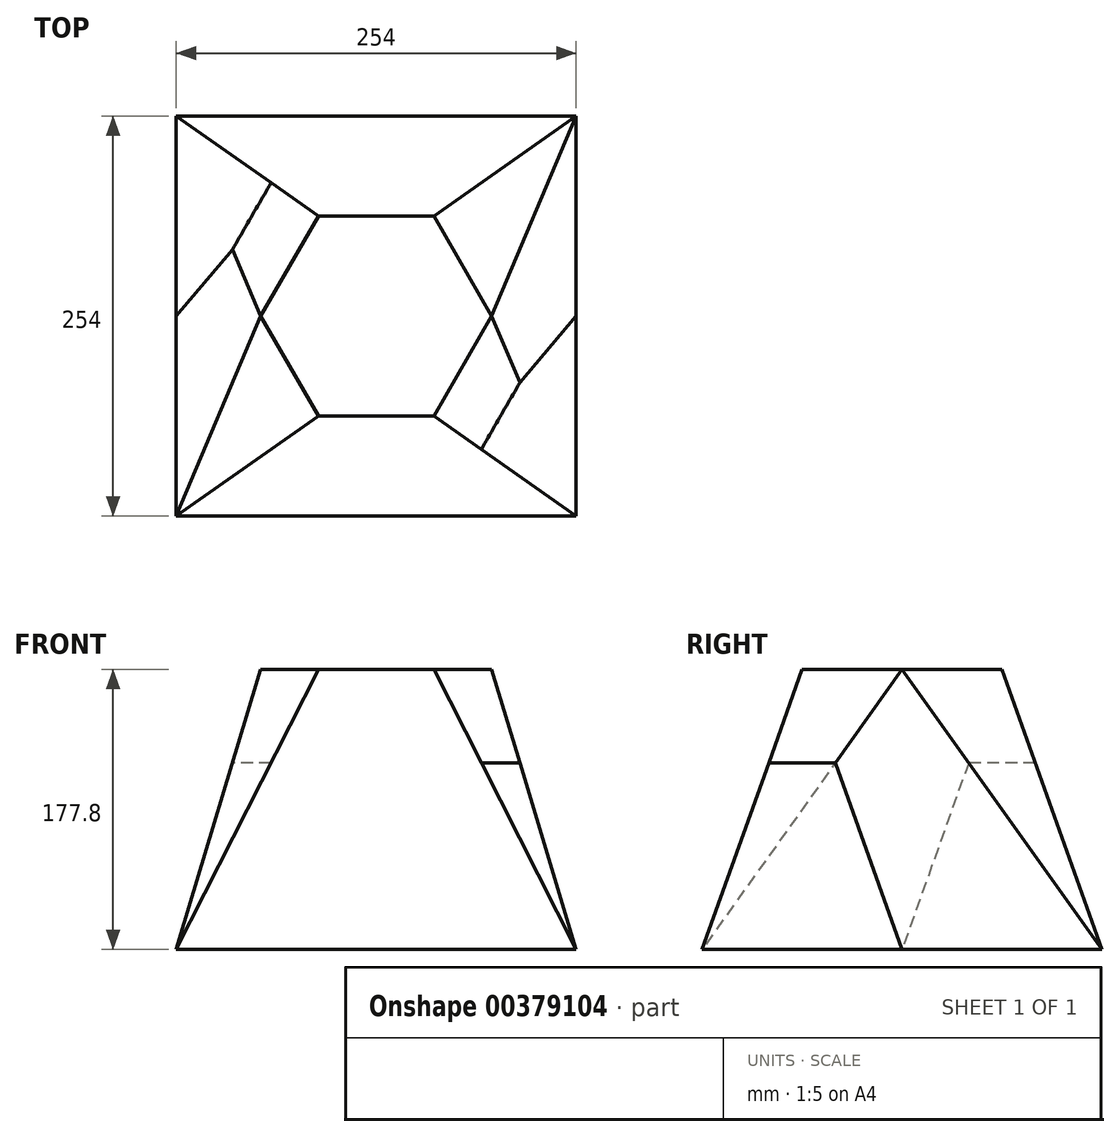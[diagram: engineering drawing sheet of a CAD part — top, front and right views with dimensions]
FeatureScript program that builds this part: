
annotation { "Feature Type Name" : "Feature", "Feature Type Description" : "" }
export const myFeature = defineFeature(function(context is Context, id is Id, definition is map)
    precondition{}
    {
        {
            var Q0;
            Q0=qCreatedBy(makeId("Top.planeOp"),FACE);
            var sketch = newSketch(context, id + "F0", { "sketchPlane" : qUnion([Q0])});
            skLineSegment(sketch, "E0.bottom", {"start": v(-127, 127) * mm, "end": v(127, 127) * mm});
            skLineSegment(sketch, "E0.top", {"start": v(-127, -127) * mm, "end": v(127, -127) * mm});
            skLineSegment(sketch, "E0.left", {"start": v(-127, 127) * mm, "end": v(-127, -127) * mm});
            skLineSegment(sketch, "E0.right", {"start": v(127, 127) * mm, "end": v(127, -127) * mm});
            skSolve(sketch);
        }
        {
            var Q0;
            Q0=makeQuery(id+"F0.imprint","IMPRINT",FACE,{"disambiguationData":[TD([[makeQuery(id+"F0.imprint","IMPRINT",EDGE,{"derivedFrom":sQuery(id+"F0.wireOp",EDGE,"E0.bottom")}),-1.0]])]});
            cPlane(context, id + "F1", {"entities" : qUnion([Q0]), "cplaneType" : CPlaneType.OFFSET, "offset" : 177.8 * mm, "width" : 152.4 * mm, "height" : 152.4 * mm});
        }
        {
            var Q0;
            Q0=qCreatedBy(id+"F1.planeOp",FACE);
            var sketch = newSketch(context, id + "F2", { "sketchPlane" : qUnion([Q0])});
            skCircle(sketch, "E1.cCircle", {"center": v(0, 0) * mm, "radius": 63.5 * mm, "construction": true});
            skLineSegment(sketch, "E1.0", {"start": v(36.66, -63.5) * mm, "end": v(-36.66, -63.5) * mm});
            skLineSegment(sketch, "E1.1", {"start": v(-36.66, -63.5) * mm, "end": v(-73.32, 0) * mm, "construction": true});
            skLineSegment(sketch, "E1.2", {"start": v(-73.32, 0) * mm, "end": v(-36.66, 63.5) * mm, "construction": true});
            skLineSegment(sketch, "E1.3", {"start": v(-36.66, 63.5) * mm, "end": v(36.66, 63.5) * mm});
            skLineSegment(sketch, "E1.4", {"start": v(36.66, 63.5) * mm, "end": v(73.32, 0) * mm, "construction": true});
            skLineSegment(sketch, "E1.5", {"start": v(73.32, 0) * mm, "end": v(36.66, -63.5) * mm, "construction": true});
            skPoint(sketch, "E1.0.midPoint", {"position": v(0, -63.5) * mm});
            skLineSegment(sketch, "E2.bottom", {"start": v(73.32, -63.5) * mm, "end": v(-73.32, -63.5) * mm});
            skLineSegment(sketch, "E2.top", {"start": v(73.32, 63.5) * mm, "end": v(-73.32, 63.5) * mm});
            skLineSegment(sketch, "E2.left", {"start": v(73.32, -63.5) * mm, "end": v(73.32, 63.5) * mm});
            skLineSegment(sketch, "E2.right", {"start": v(-73.32, -63.5) * mm, "end": v(-73.32, 63.5) * mm});
            skSolve(sketch);
        }
        {
            var Q0;
            {var subQ0=sQuery(id+"F2.wireOp",EDGE,"E2.left");Q0=makeQuery(id+"F2.imprint","IMPRINT",FACE,{"disambiguationData":[TD([[makeQuery(id+"F2.imprint","IMPRINT",EDGE,{"derivedFrom":subQ0}),1.0]])]});}
            var Q1;
            Q1=makeQuery(id+"F0.imprint","IMPRINT",FACE,{"disambiguationData":[TD([[makeQuery(id+"F0.imprint","IMPRINT",EDGE,{"derivedFrom":sQuery(id+"F0.wireOp",EDGE,"E0.bottom")}),-1.0]])]});
            loft(context, id + "F3", {"sheetProfilesArray" : [{ "sheetProfileEntities" : qUnion([Q0]) }, { "sheetProfileEntities" : qUnion([Q1]) }]});
        }
        {
            var Q0;
            Q0=qCreatedBy(id+"F1.planeOp",FACE);
            var sketch = newSketch(context, id + "F4", { "sketchPlane" : qUnion([Q0])});
            skCircle(sketch, "E3.cCircle", {"center": v(0, 0) * mm, "radius": 63.5 * mm, "construction": true});
            skLineSegment(sketch, "E3.0", {"start": v(36.66, -63.5) * mm, "end": v(-36.66, -63.5) * mm});
            skLineSegment(sketch, "E3.1", {"start": v(-36.66, -63.5) * mm, "end": v(-73.32, 0) * mm});
            skLineSegment(sketch, "E3.2", {"start": v(-73.32, 0) * mm, "end": v(-36.66, 63.5) * mm});
            skLineSegment(sketch, "E3.3", {"start": v(-36.66, 63.5) * mm, "end": v(36.66, 63.5) * mm});
            skLineSegment(sketch, "E3.4", {"start": v(36.66, 63.5) * mm, "end": v(73.32, 0) * mm});
            skLineSegment(sketch, "E3.5", {"start": v(73.32, 0) * mm, "end": v(36.66, -63.5) * mm});
            skPoint(sketch, "E3.0.midPoint", {"position": v(0, -63.5) * mm});
            skLineSegment(sketch, "E4.bottom", {"start": v(73.32, -63.5) * mm, "end": v(-73.32, -63.5) * mm});
            skLineSegment(sketch, "E4.top", {"start": v(73.32, 63.5) * mm, "end": v(-73.32, 63.5) * mm});
            skLineSegment(sketch, "E4.left", {"start": v(73.32, -63.5) * mm, "end": v(73.32, 63.5) * mm});
            skLineSegment(sketch, "E4.right", {"start": v(-73.32, -63.5) * mm, "end": v(-73.32, 63.5) * mm});
            skSolve(sketch);
        }
        {
            var Q1;
            {var subQ0=sQuery(id+"F4.wireOp",EDGE,"E3.4");Q1=makeQuery(id+"F4.imprint","IMPRINT",FACE,{"disambiguationData":[TD([[makeQuery(id+"F4.imprint","IMPRINT",EDGE,{"derivedFrom":subQ0}),1.0]])]});}
            var Q2;
            Q2=sQuery(id+"F0.wireOp",VERTEX,"E0.right.start");
            loft(context, id + "F5", {"sheetProfilesArray" : [{ "sheetProfileEntities" : qUnion([Q1]) }, { "sheetProfileEntities" : qUnion([Q2]) }]});
        }
        {
            var Q1;
            {var subQ0=sQuery(id+"F4.wireOp",EDGE,"E3.2");Q1=makeQuery(id+"F4.imprint","IMPRINT",FACE,{"disambiguationData":[TD([[makeQuery(id+"F4.imprint","IMPRINT",EDGE,{"derivedFrom":subQ0}),1.0]])]});}
            var Q2;
            Q2=sQuery(id+"F0.wireOp",VERTEX,"E0.left.start");
            loft(context, id + "F6", {"sheetProfilesArray" : [{ "sheetProfileEntities" : qUnion([Q1]) }, { "sheetProfileEntities" : qUnion([Q2]) }]});
        }
        {
            var Q1;
            {var subQ0=sQuery(id+"F4.wireOp",EDGE,"E3.1");Q1=makeQuery(id+"F4.imprint","IMPRINT",FACE,{"disambiguationData":[TD([[makeQuery(id+"F4.imprint","IMPRINT",EDGE,{"derivedFrom":subQ0}),1.0]])]});}
            var Q2;
            Q2=sQuery(id+"F0.wireOp",VERTEX,"E0.left.end");
            loft(context, id + "F7", {"sheetProfilesArray" : [{ "sheetProfileEntities" : qUnion([Q1]) }, { "sheetProfileEntities" : qUnion([Q2]) }]});
        }
        {
            var Q1;
            {var subQ0=sQuery(id+"F4.wireOp",EDGE,"E3.5");Q1=makeQuery(id+"F4.imprint","IMPRINT",FACE,{"disambiguationData":[TD([[makeQuery(id+"F4.imprint","IMPRINT",EDGE,{"derivedFrom":subQ0}),1.0]])]});}
            var Q2;
            Q2=sQuery(id+"F0.wireOp",VERTEX,"E0.right.end");
            loft(context, id + "F8", {"sheetProfilesArray" : [{ "sheetProfileEntities" : qUnion([Q1]) }, { "sheetProfileEntities" : qUnion([Q2]) }]});
        }
        {
            var Q0;
            {var subQ0=sQuery(id+"F4.wireOp",EDGE,"E3.4");Q0=makeQuery(id+"F5.opLoft","SWEPT_BODY",BODY,{"disambiguationData":[OSD([sQuery(id+"F0.wireOp",VERTEX,"E0.right.start"),makeQuery(id+"F4.imprint","IMPRINT",FACE,{"disambiguationData":[TD([[makeQuery(id+"F4.imprint","IMPRINT",EDGE,{"derivedFrom":subQ0}),1.0]])]})])]});}
            var Q1;
            {var subQ0=sQuery(id+"F4.wireOp",EDGE,"E3.2");Q1=makeQuery(id+"F6.opLoft","SWEPT_BODY",BODY,{"disambiguationData":[OSD([sQuery(id+"F0.wireOp",VERTEX,"E0.left.start"),makeQuery(id+"F4.imprint","IMPRINT",FACE,{"disambiguationData":[TD([[makeQuery(id+"F4.imprint","IMPRINT",EDGE,{"derivedFrom":subQ0}),1.0]])]})])]});}
            var Q2;
            {var subQ0=sQuery(id+"F4.wireOp",EDGE,"E3.1");Q2=makeQuery(id+"F7.opLoft","SWEPT_BODY",BODY,{"disambiguationData":[OSD([sQuery(id+"F0.wireOp",VERTEX,"E0.left.end"),makeQuery(id+"F4.imprint","IMPRINT",FACE,{"disambiguationData":[TD([[makeQuery(id+"F4.imprint","IMPRINT",EDGE,{"derivedFrom":subQ0}),1.0]])]})])]});}
            var Q3;
            {var subQ0=sQuery(id+"F4.wireOp",EDGE,"E3.5");Q3=makeQuery(id+"F8.opLoft","SWEPT_BODY",BODY,{"disambiguationData":[OSD([sQuery(id+"F0.wireOp",VERTEX,"E0.right.end"),makeQuery(id+"F4.imprint","IMPRINT",FACE,{"disambiguationData":[TD([[makeQuery(id+"F4.imprint","IMPRINT",EDGE,{"derivedFrom":subQ0}),1.0]])]})])]});}
            var Q4;
            {var subQ0=sQuery(id+"F2.wireOp",EDGE,"E2.left");Q4=makeQuery(id+"F3.opLoft","SWEPT_BODY",BODY,{"disambiguationData":[OSD([makeQuery(id+"F0.imprint","IMPRINT",FACE,{"disambiguationData":[TD([[makeQuery(id+"F0.imprint","IMPRINT",EDGE,{"derivedFrom":sQuery(id+"F0.wireOp",EDGE,"E0.bottom")}),-1.0]])]}),makeQuery(id+"F2.imprint","IMPRINT",FACE,{"disambiguationData":[TD([[makeQuery(id+"F2.imprint","IMPRINT",EDGE,{"derivedFrom":subQ0}),1.0]])]})])]});}
            booleanBodies(context, id + "F9", {"operationType" : BooleanOperationType.SUBTRACTION, "tools" : qUnion([Q0, Q1, Q2, Q3]), "targets" : qUnion([Q4])});
        }
    });
